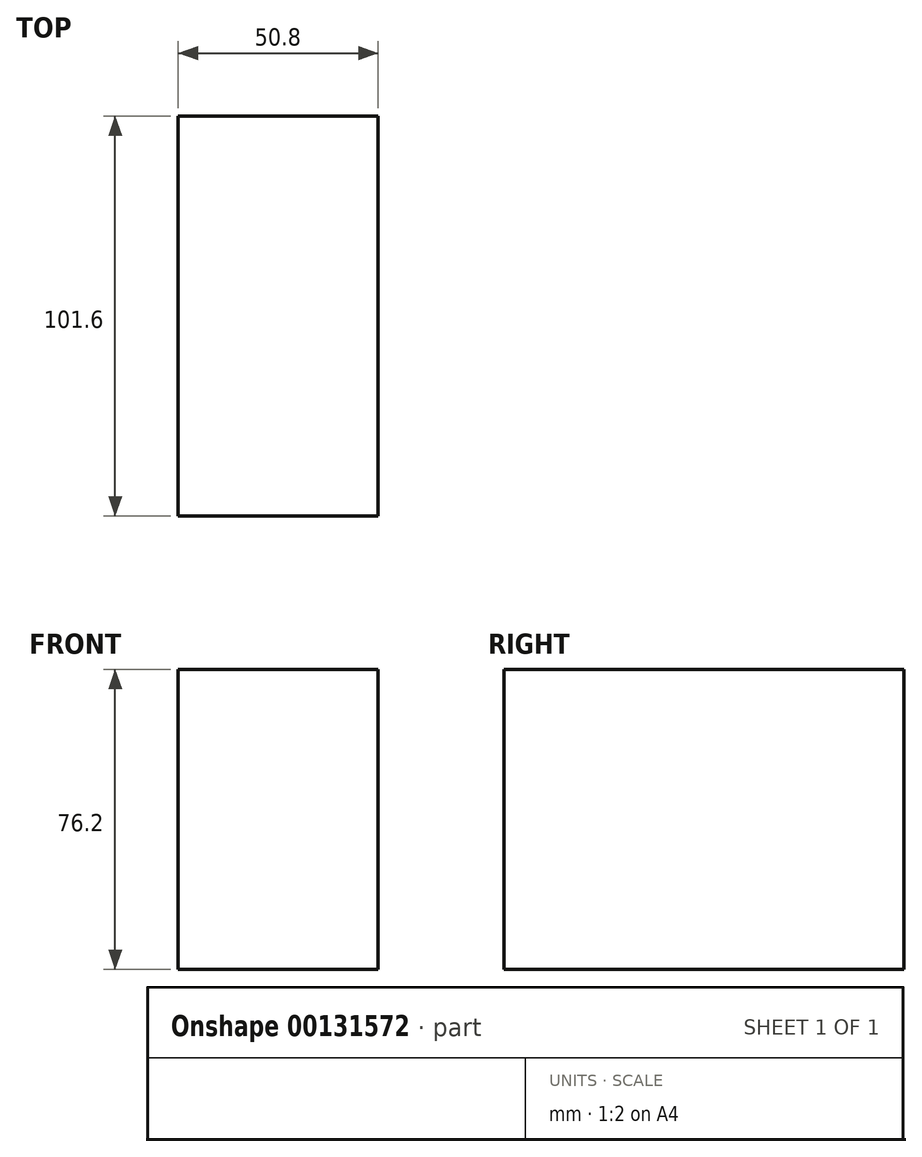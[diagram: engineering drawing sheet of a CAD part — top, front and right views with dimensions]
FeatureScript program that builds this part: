
annotation { "Feature Type Name" : "Feature", "Feature Type Description" : "" }
export const myFeature = defineFeature(function(context is Context, id is Id, definition is map)
    precondition{}
    {
        {
            var Q0;
            Q0=qCreatedBy(makeId("Front.planeOp"),FACE);
            var sketch = newSketch(context, id + "F0", { "sketchPlane" : qUnion([Q0])});
            skLineSegment(sketch, "E0.bottom", {"start": v(-25.4, 38.1) * mm, "end": v(25.4, 38.1) * mm});
            skLineSegment(sketch, "E0.top", {"start": v(-25.4, -38.1) * mm, "end": v(25.4, -38.1) * mm});
            skLineSegment(sketch, "E0.left", {"start": v(-25.4, 38.1) * mm, "end": v(-25.4, -38.1) * mm});
            skLineSegment(sketch, "E0.right", {"start": v(25.4, 38.1) * mm, "end": v(25.4, -38.1) * mm});
            skPoint(sketch, "E0.middle", {"position": v(0, 0) * mm});
            skSolve(sketch);
        }
        {
            var Q0;
            Q0=makeQuery(id+"F0.imprint","IMPRINT",FACE,{"disambiguationData":[TD([[makeQuery(id+"F0.imprint","IMPRINT",EDGE,{"derivedFrom":sQuery(id+"F0.wireOp",EDGE,"E0.bottom")}),-1.0]])]});
            extrude(context, id + "F1", {"entities" : qUnion([Q0]), "depth" : 101.6 * mm});
        }
    });
